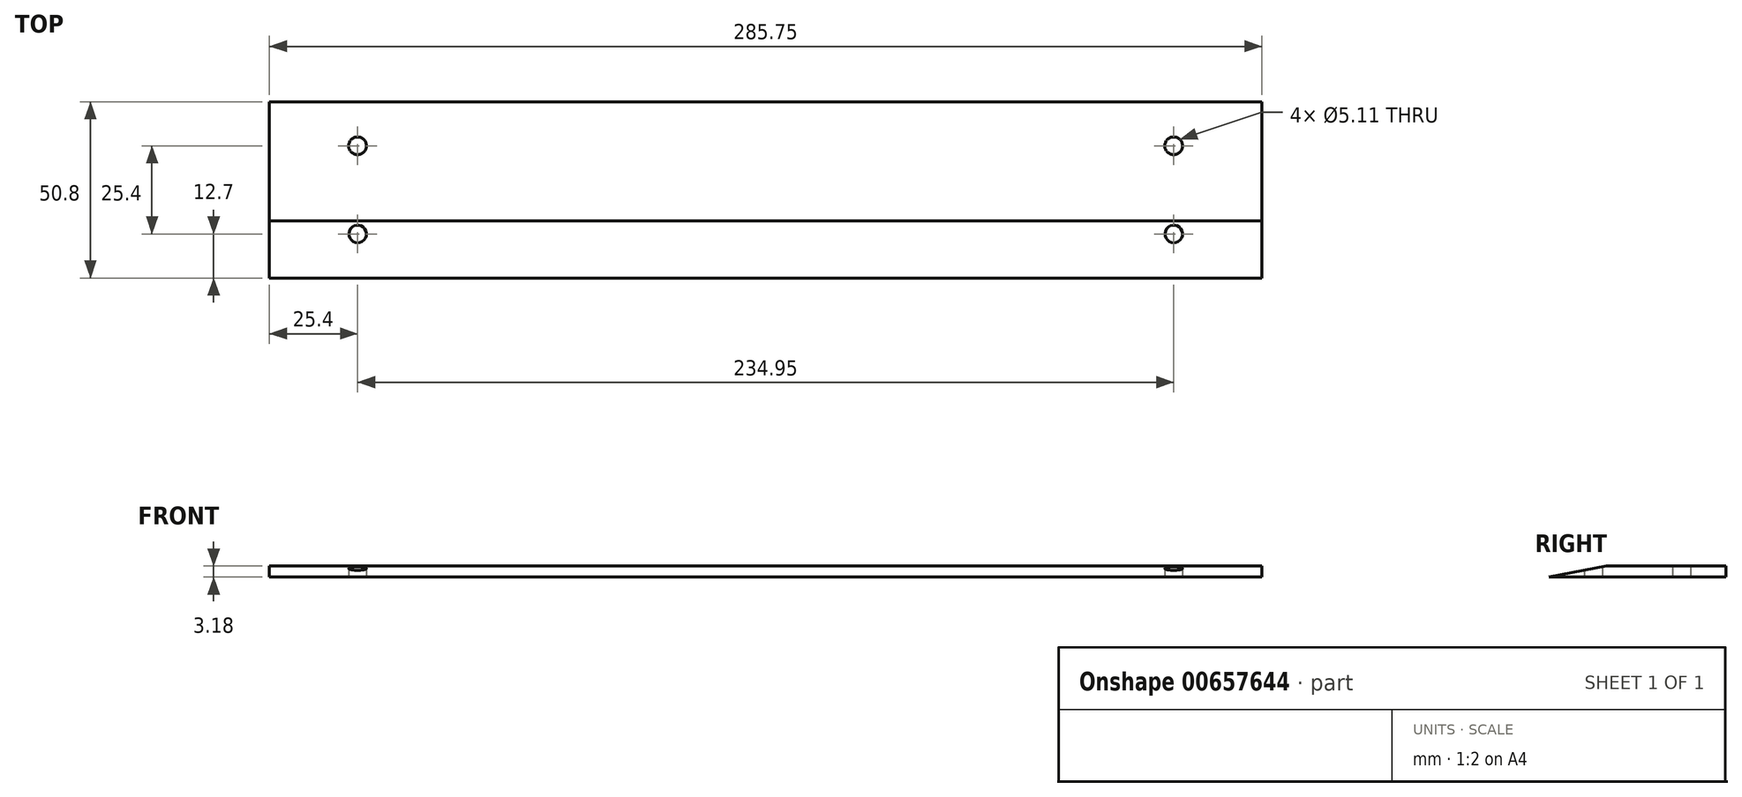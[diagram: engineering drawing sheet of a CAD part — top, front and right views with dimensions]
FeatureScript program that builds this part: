
annotation { "Feature Type Name" : "Feature", "Feature Type Description" : "" }
export const myFeature = defineFeature(function(context is Context, id is Id, definition is map)
    precondition{}
    {
        {
            var Q0;
            Q0=qCreatedBy(makeId("Top.planeOp"),FACE);
            var sketch = newSketch(context, id + "F0", { "sketchPlane" : qUnion([Q0])});
            skLineSegment(sketch, "E0.bottom", {"start": v(0, 0) * mm, "end": v(285.75, 0) * mm});
            skLineSegment(sketch, "E0.top", {"start": v(0, -50.8) * mm, "end": v(285.75, -50.8) * mm});
            skLineSegment(sketch, "E0.left", {"start": v(0, 0) * mm, "end": v(0, -50.8) * mm});
            skLineSegment(sketch, "E0.right", {"start": v(285.75, 0) * mm, "end": v(285.75, -50.8) * mm});
            skCircle(sketch, "E1", {"center": v(25.4, -12.7) * mm, "radius": 2.55 * mm});
            skCircle(sketch, "E2", {"center": v(25.4, -38.1) * mm, "radius": 2.55 * mm});
            skCircle(sketch, "E3", {"center": v(260.35, -12.7) * mm, "radius": 2.55 * mm});
            skCircle(sketch, "E4", {"center": v(260.35, -38.1) * mm, "radius": 2.55 * mm});
            skSolve(sketch);
        }
        {
            var Q0;
            Q0=makeQuery(id+"F0.imprint","IMPRINT",FACE,{"disambiguationData":[TD([[makeQuery(id+"F0.imprint","IMPRINT",EDGE,{"derivedFrom":sQuery(id+"F0.wireOp",EDGE,"E0.bottom")}),-1.0]])]});
            extrude(context, id + "F1", {"entities" : qUnion([Q0]), "depth" : 3.17 * mm, "offsetDistance" : 25.4 * mm});
        }
        {
            var Q0;
            Q0=makeQuery(id+"F1.opExtrude","SWEPT_FACE",FACE,{"disambiguationData":[OSD([sQuery(id+"F0.wireOp",EDGE,"E0.right")])]});
            var sketch = newSketch(context, id + "F2", { "sketchPlane" : qUnion([Q0])});
            skLineSegment(sketch, "E5", {"start": v(-50.8, 0) * mm, "end": v(-34.37, 3.18) * mm});
            skSolve(sketch);
        }
        {
            var Q0;
            {var subQ0=sQuery(id+"F2.wireOp",EDGE,"E5");Q0=makeQuery(id+"F2.imprint","IMPRINT",FACE,{"disambiguationData":[TD([[makeQuery(id+"F2.imprint","IMPRINT",EDGE,{"derivedFrom":subQ0}),1.0]])]});}
            extrude(context, id + "F3", {"entities" : qUnion([Q0]), "operationType" : NewBodyOperationType.REMOVE, "endBound" : BoundingType.THROUGH_ALL, "oppositeDirection" : true, "depth" : 25.4 * mm, "offsetDistance" : 25.4 * mm});
        }
    });
